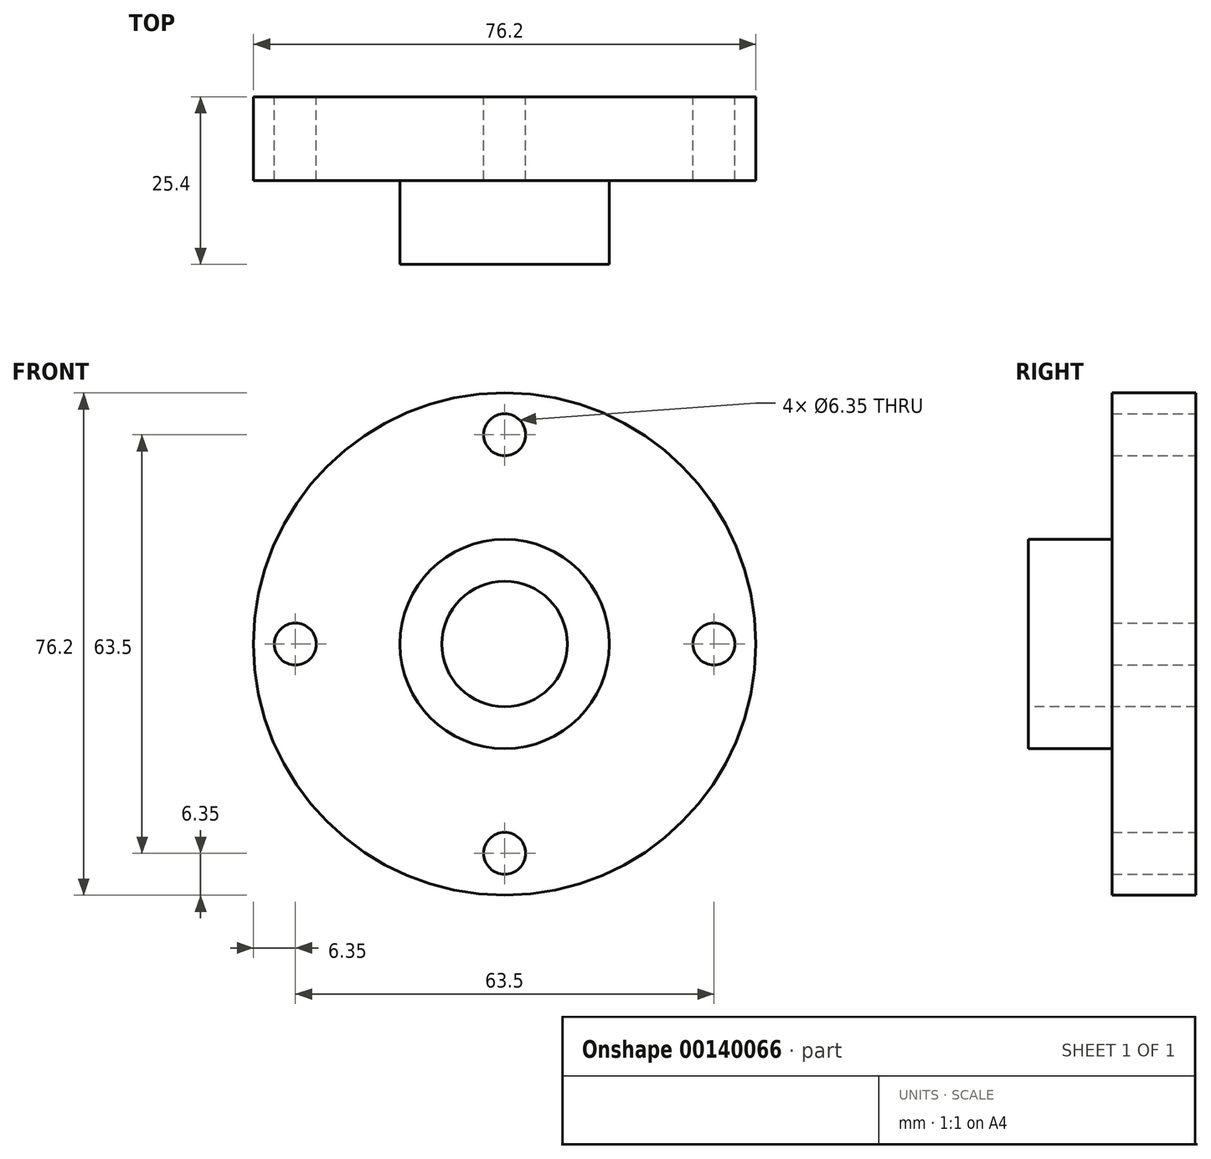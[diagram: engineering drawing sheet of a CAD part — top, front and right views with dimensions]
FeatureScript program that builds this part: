
annotation { "Feature Type Name" : "Feature", "Feature Type Description" : "" }
export const myFeature = defineFeature(function(context is Context, id is Id, definition is map)
    precondition{}
    {
        {
            var Q0;
            Q0=qCreatedBy(makeId("Front.planeOp"),FACE);
            var sketch = newSketch(context, id + "F0", { "sketchPlane" : qUnion([Q0])});
            skCircle(sketch, "E0", {"center": v(0, 0) * mm, "radius": 38.1 * mm});
            skCircle(sketch, "E1", {"center": v(0, 31.75) * mm, "radius": 3.18 * mm});
            skCircle(sketch, "E2", {"center": v(31.75, 0) * mm, "radius": 3.18 * mm});
            skCircle(sketch, "E3", {"center": v(0, -31.75) * mm, "radius": 3.18 * mm});
            skCircle(sketch, "E4", {"center": v(-31.75, 0) * mm, "radius": 3.18 * mm});
            skSolve(sketch);
        }
        {
            var Q0;
            Q0 = qSketchRegion(id + "F0", true);
            extrude(context, id + "F1", {"entities" : qUnion([Q0]), "depth" : 12.7 * mm});
        }
        {
            var Q0;
            Q0=makeQuery(id+"F1.opExtrude","CAP_FACE",FACE,{"disambiguationData":[OSD([sQuery(id+"F0.wireOp",EDGE,"E0"),sQuery(id+"F0.wireOp",EDGE,"E1"),sQuery(id+"F0.wireOp",EDGE,"E2"),sQuery(id+"F0.wireOp",EDGE,"E3"),sQuery(id+"F0.wireOp",EDGE,"E4")])],"isStart":false});
            var sketch = newSketch(context, id + "F2", { "sketchPlane" : qUnion([Q0])});
            skCircle(sketch, "E5.0.0", {"center": v(0, 0) * mm, "radius": 38.1 * mm});
            skCircle(sketch, "E6", {"center": v(0, 0) * mm, "radius": 15.88 * mm});
            skSolve(sketch);
        }
        {
            var Q0;
            Q0=makeQuery(id+"F2.imprint","IMPRINT",FACE,{"disambiguationData":[TD([[makeQuery(id+"F2.imprint","IMPRINT",EDGE,{"derivedFrom":sQuery(id+"F2.wireOp",EDGE,"E6")}),1.0]])]});
            extrude(context, id + "F3", {"entities" : qUnion([Q0]), "operationType" : NewBodyOperationType.ADD, "depth" : 12.7 * mm});
        }
        {
            var Q0;
            Q0=makeQuery(id+"F3.opExtrude","CAP_FACE",FACE,{"disambiguationData":[OSD([sQuery(id+"F2.wireOp",EDGE,"E6")])],"isStart":false});
            var sketch = newSketch(context, id + "F4", { "sketchPlane" : qUnion([Q0])});
            skCircle(sketch, "E7", {"center": v(0, 0) * mm, "radius": 9.53 * mm});
            skSolve(sketch);
        }
        {
            var Q0;
            Q0 = qSketchRegion(id + "F4", true);
            extrude(context, id + "F5", {"entities" : qUnion([Q0]), "operationType" : NewBodyOperationType.REMOVE, "endBound" : BoundingType.THROUGH_ALL, "oppositeDirection" : true, "depth" : 25.4 * mm});
        }
    });
